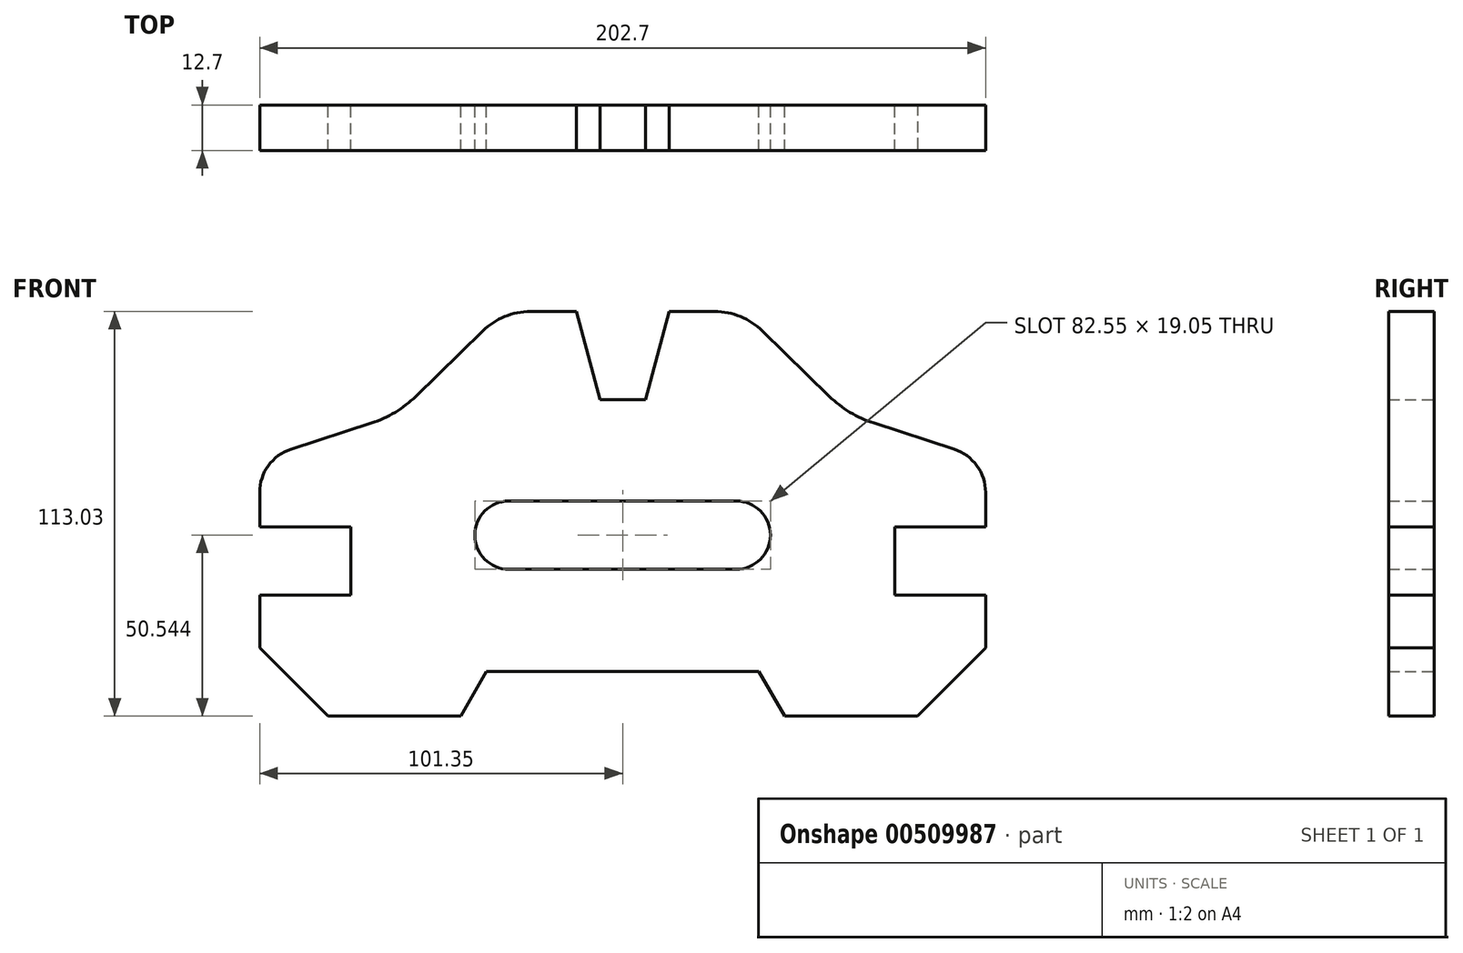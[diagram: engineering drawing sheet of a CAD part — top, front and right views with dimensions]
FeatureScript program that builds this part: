
annotation { "Feature Type Name" : "Feature", "Feature Type Description" : "" }
export const myFeature = defineFeature(function(context is Context, id is Id, definition is map)
    precondition{}
    {
        {
            var Q0;
            Q0=qCreatedBy(makeId("Front.planeOp"),FACE);
            var sketch = newSketch(context, id + "F0", { "sketchPlane" : qUnion([Q0])});
            skLineSegment(sketch, "E0", {"start": v(6.35, 84.04) * mm, "end": v(12.95, 108.68) * mm});
            skLineSegment(sketch, "E1", {"start": v(0, 8.1) * mm, "end": v(38.03, 8.1) * mm});
            skLineSegment(sketch, "E2", {"start": v(38.03, 8.1) * mm, "end": v(45.21, -4.35) * mm});
            skLineSegment(sketch, "E3", {"start": v(-31.75, 55.72) * mm, "end": v(31.75, 55.72) * mm});
            skLineSegment(sketch, "E4", {"start": v(-31.75, 36.67) * mm, "end": v(31.75, 36.67) * mm});
            skArc(sketch, "E5", {"start": v(31.75, 55.72) * mm, "mid": v(41.27, 46.2) * mm, "end": v(31.75, 36.67) * mm});
            skArc(sketch, "E6", {"start": v(-31.75, 55.72) * mm, "mid": v(-41.28, 46.2) * mm, "end": v(-31.75, 36.67) * mm});
            skLineSegment(sketch, "E7", {"start": v(12.95, 108.68) * mm, "end": v(25.74, 108.68) * mm});
            skArc(sketch, "E8", {"start": v(25.74, 108.68) * mm, "mid": v(32.92, 107.27) * mm, "end": v(39.05, 103.26) * mm});
            skLineSegment(sketch, "E9", {"start": v(39.05, 103.26) * mm, "end": v(57.75, 85) * mm});
            skArc(sketch, "E10", {"start": v(57.75, 85) * mm, "mid": v(63.5, 80.55) * mm, "end": v(70.1, 77.53) * mm});
            skLineSegment(sketch, "E11", {"start": v(70.1, 77.53) * mm, "end": v(92.58, 70.2) * mm});
            skArc(sketch, "E12", {"start": v(92.58, 70.2) * mm, "mid": v(98.92, 65.6) * mm, "end": v(101.35, 58.13) * mm});
            skLineSegment(sketch, "E13", {"start": v(101.35, 58.13) * mm, "end": v(101.35, 48.48) * mm});
            skLineSegment(sketch, "E14", {"start": v(101.35, 29.43) * mm, "end": v(75.95, 29.43) * mm});
            skLineSegment(sketch, "E15", {"start": v(75.95, 29.43) * mm, "end": v(75.95, 48.48) * mm});
            skLineSegment(sketch, "E16", {"start": v(75.95, 48.48) * mm, "end": v(101.35, 48.48) * mm});
            skLineSegment(sketch, "E17", {"start": v(0, 108.68) * mm, "end": v(0, -107.82) * mm, "construction": true});
            skLineSegment(sketch, "E18.MirrorCS", {"start": v(-6.35, 84.04) * mm, "end": v(-12.95, 108.68) * mm});
            skArc(sketch, "E19.MirrorCS", {"start": v(-25.74, 108.68) * mm, "mid": v(-32.92, 107.27) * mm, "end": v(-39.05, 103.26) * mm});
            skLineSegment(sketch, "E20.MirrorCS", {"start": v(-39.05, 103.26) * mm, "end": v(-57.75, 85) * mm});
            skArc(sketch, "E21.MirrorCS", {"start": v(-57.75, 85) * mm, "mid": v(-63.5, 80.55) * mm, "end": v(-70.1, 77.53) * mm});
            skLineSegment(sketch, "E22.MirrorCS", {"start": v(-70.1, 77.53) * mm, "end": v(-92.58, 70.2) * mm});
            skArc(sketch, "E23.MirrorCS", {"start": v(-92.58, 70.2) * mm, "mid": v(-98.92, 65.6) * mm, "end": v(-101.35, 58.13) * mm});
            skLineSegment(sketch, "E24.MirrorCS", {"start": v(-101.35, 58.13) * mm, "end": v(-101.35, 48.48) * mm});
            skLineSegment(sketch, "E25.MirrorCS", {"start": v(-75.95, 48.48) * mm, "end": v(-101.35, 48.48) * mm});
            skLineSegment(sketch, "E26.MirrorCS", {"start": v(-75.95, 29.43) * mm, "end": v(-75.95, 48.48) * mm});
            skLineSegment(sketch, "E27.MirrorCS", {"start": v(-101.35, 29.43) * mm, "end": v(-75.95, 29.43) * mm});
            skLineSegment(sketch, "E28.MirrorCS", {"start": v(-38.03, 8.1) * mm, "end": v(-45.21, -4.35) * mm});
            skLineSegment(sketch, "E29.MirrorCS", {"start": v(0, 8.1) * mm, "end": v(-38.03, 8.1) * mm});
            skLineSegment(sketch, "E30", {"start": v(-25.74, 108.68) * mm, "end": v(-12.95, 108.68) * mm});
            skLineSegment(sketch, "E31", {"start": v(-6.35, 84.04) * mm, "end": v(6.35, 84.04) * mm});
            skLineSegment(sketch, "E32", {"start": v(-38.03, 8.1) * mm, "end": v(-38.03, -60.53) * mm, "construction": true});
            skLineSegment(sketch, "E33", {"start": v(38.03, 8.1) * mm, "end": v(38.03, -59.56) * mm, "construction": true});
            skLineSegment(sketch, "E34", {"start": v(6.35, 84.04) * mm, "end": v(6.35, 133.67) * mm, "construction": true});
            skLineSegment(sketch, "E35", {"start": v(-6.35, 84.04) * mm, "end": v(-6.35, 139.53) * mm, "construction": true});
            skLineSegment(sketch, "E36", {"start": v(-101.35, 29.43) * mm, "end": v(-101.35, -4.35) * mm});
            skLineSegment(sketch, "E37", {"start": v(-101.35, -4.35) * mm, "end": v(-45.21, -4.35) * mm});
            skLineSegment(sketch, "E38", {"start": v(101.35, 29.43) * mm, "end": v(101.35, -4.35) * mm});
            skLineSegment(sketch, "E39", {"start": v(101.35, -4.35) * mm, "end": v(45.21, -4.35) * mm});
            skSolve(sketch);
        }
        {
            var Q0;
            Q0 = qSketchRegion(id + "F0", true);
            extrude(context, id + "F1", {"entities" : qUnion([Q0]), "depth" : 12.7 * mm, "offsetDistance" : 25.4 * mm});
        }
        {
            var Q0;
            Q0=makeQuery(id+"F1.opExtrude","SWEPT_EDGE",EDGE,{"disambiguationData":[OSD([sQuery(id+"F0.wireOp",EDGE,"E36"),sQuery(id+"F0.wireOp",EDGE,"E37")])]});
            var Q1;
            Q1=makeQuery(id+"F1.opExtrude","SWEPT_EDGE",EDGE,{"disambiguationData":[OSD([sQuery(id+"F0.wireOp",EDGE,"E38"),sQuery(id+"F0.wireOp",EDGE,"E39")])]});
            chamfer(context, id + "F2", {"entities" : qUnion([Q0, Q1]), "width" : 19.05 * mm, "tangentPropagation" : true});
        }
    });
